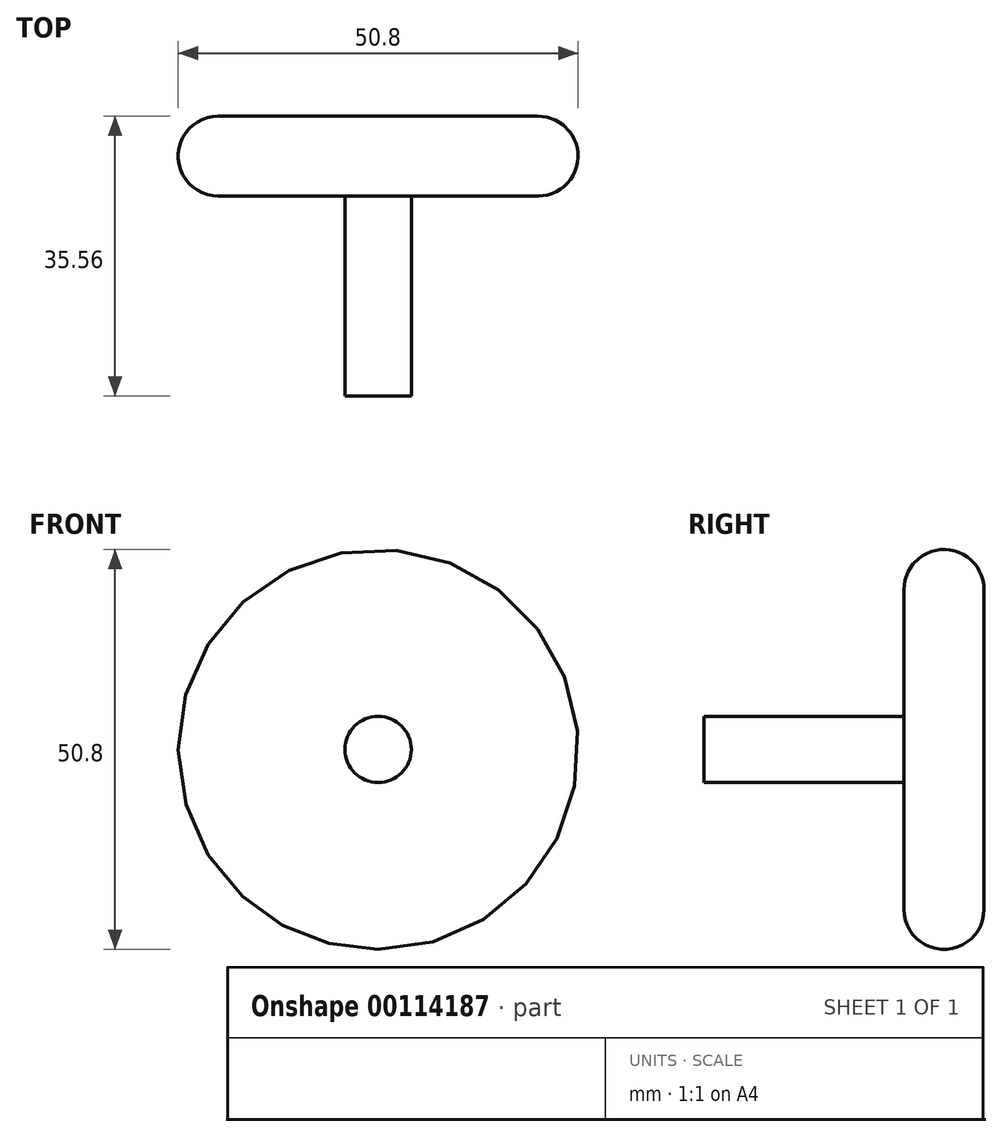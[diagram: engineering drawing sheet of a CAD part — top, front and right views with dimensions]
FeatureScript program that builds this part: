
annotation { "Feature Type Name" : "Feature", "Feature Type Description" : "" }
export const myFeature = defineFeature(function(context is Context, id is Id, definition is map)
    precondition{}
    {
        {
            var Q0;
            Q0=qCreatedBy(makeId("Front.planeOp"),FACE);
            var sketch = newSketch(context, id + "F0", { "sketchPlane" : qUnion([Q0])});
            skCircle(sketch, "E0", {"center": v(0, 0) * mm, "radius": 25.4 * mm});
            skSolve(sketch);
        }
        {
            var Q0;
            Q0 = qSketchRegion(id + "F0", true);
            extrude(context, id + "F1", {"entities" : qUnion([Q0]), "depth" : 10.16 * mm});
        }
        {
            var Q0;
            Q0=makeQuery(id+"F1.opExtrude","CAP_EDGE",EDGE,{"disambiguationData":[OSD([sQuery(id+"F0.wireOp",EDGE,"E0")])],"isStart":false});
            fillet(context, id + "F2", {"entities" : qUnion([Q0]), "radius" : 5.08 * mm, "tangentPropagation" : true, "allowEdgeOverflow" : false});
        }
        {
            var Q0;
            Q0=makeQuery(id+"F1.opExtrude","CAP_EDGE",EDGE,{"disambiguationData":[OSD([sQuery(id+"F0.wireOp",EDGE,"E0")])],"isStart":true});
            fillet(context, id + "F3", {"entities" : qUnion([Q0]), "radius" : 5.08 * mm, "tangentPropagation" : true, "allowEdgeOverflow" : false});
        }
        {
            var Q0;
            Q0=makeQuery(id+"F1.opExtrude","CAP_FACE",FACE,{"disambiguationData":[OSD([sQuery(id+"F0.wireOp",EDGE,"E0")])],"isStart":false});
            var sketch = newSketch(context, id + "F4", { "sketchPlane" : qUnion([Q0])});
            skCircle(sketch, "E1", {"center": v(0, 0) * mm, "radius": 4.22 * mm});
            skSolve(sketch);
        }
        {
            var Q0;
            Q0=makeQuery(id+"F4.imprint","IMPRINT",FACE,{"disambiguationData":[TD([[makeQuery(id+"F4.imprint","IMPRINT",EDGE,{"derivedFrom":sQuery(id+"F4.wireOp",EDGE,"E1")}),1.0]])]});
            extrude(context, id + "F5", {"entities" : qUnion([Q0]), "operationType" : NewBodyOperationType.ADD, "depth" : 25.4 * mm});
        }
    });
